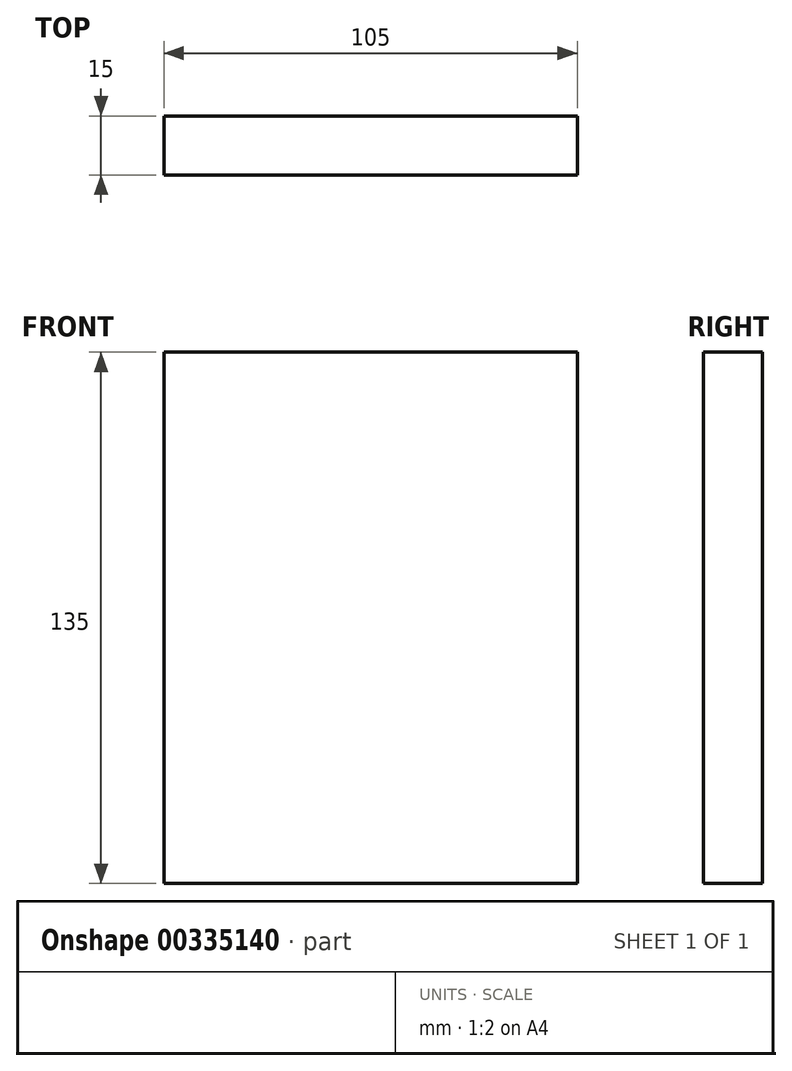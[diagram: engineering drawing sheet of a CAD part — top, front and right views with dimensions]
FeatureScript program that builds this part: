
annotation { "Feature Type Name" : "Feature", "Feature Type Description" : "" }
export const myFeature = defineFeature(function(context is Context, id is Id, definition is map)
    precondition{}
    {
        {
            var Q0;
            Q0=qCreatedBy(makeId("Front.planeOp"),FACE);
            var sketch = newSketch(context, id + "F0", { "sketchPlane" : qUnion([Q0])});
            skLineSegment(sketch, "E0.bottom", {"start": v(-52.49, 57.29) * mm, "end": v(52.51, 57.29) * mm});
            skLineSegment(sketch, "E0.top", {"start": v(-52.49, -77.71) * mm, "end": v(52.51, -77.71) * mm});
            skLineSegment(sketch, "E0.left", {"start": v(-52.49, 57.29) * mm, "end": v(-52.49, -77.71) * mm});
            skLineSegment(sketch, "E0.right", {"start": v(52.51, 57.29) * mm, "end": v(52.51, -77.71) * mm});
            skSolve(sketch);
        }
        {
            var Q0;
            Q0=makeQuery(id+"F0.imprint","IMPRINT",FACE,{"disambiguationData":[TD([[makeQuery(id+"F0.imprint","IMPRINT",EDGE,{"derivedFrom":sQuery(id+"F0.wireOp",EDGE,"E0.bottom")}),-1.0]])]});
            extrude(context, id + "F1", {"entities" : qUnion([Q0]), "depth" : 15 * mm, "offsetDistance" : 25 * mm});
        }
    });
